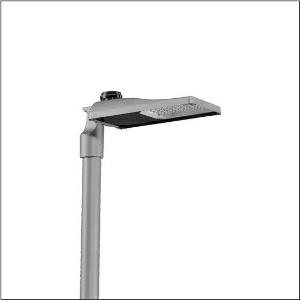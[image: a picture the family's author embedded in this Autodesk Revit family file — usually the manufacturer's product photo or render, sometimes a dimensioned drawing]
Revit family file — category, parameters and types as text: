
# Revit family: streetlight_sl_31_mini___st0_8a_5xh6c45n08ja_4560
name_source: partatom
category: Lighting Fixtures
units: mm (PartAtom-declared; Revit-internal decimal feet)

## family parameters
Cut with Voids When Loaded = No
Host = Face
Light Source = No
Part Type = Normal
Room Calculation Point = No
Round Connector Dimension = Use Diameter
Shared = No

## types (1)
- --- (1 x LED, 12590 lm, 81.1 W, 4000K)
    Apparent Load = 81 VA
    CIE Flux Codes = 41 75 97 100 100
    Color Rendering = 70
    Color Temperature = 4000K
    Default Elevation = 1800 mm
    Description = Streetlight SL 31 mini NEMA (7pin), Desk-Remote mast luminaire for post-top, side-entry; light control with lens of PMMA; light distribution: ST0.8a, direct asymmetric distribution, for standard-compliant lighting for roads and squares; LED: luminous flux: 12.590lm, light colour: 740, colour temperature: 4000K; luminous efficacy: 155,2lm/W; control: pre-setting: linear dimming characteristic, flexible luminous flux parameterisation, time-dependent luminous flux control, constant luminous flux control, intelligent temperature release in ECG and LED module, overheat protection; luminaire housing, of diecast aluminium, SITECO metallic grey (DB 702S), corrosivity category C5 high according to DIN EN ISO 12944; cover of toughened safety glass, transparent, opened without tools; mast flange of diecast aluminium, SITECO metallic grey (DB 702S), spigot size: 76/60mm, mast flange included unmounted; with cable H07RN-F 3x 1.5mm², cable length: 10,5m, connection cable pre-assembled; mains connection: 220..240V, AC, 50/60Hz; power consumption (at start of service life): 81,1W / (at end of service life): 88,3W / (with reduced operation 50%): 36,4W; protection rating (complete): IP66; insulation class (complete): insulation class I (protective earthing); impact resistance: IK10; certification: CE, ENEC, ENEC+, VDE, UKCA; permissible operating ambient temperature for outdoor applications: -40..+50°C; packaging unit: 1 piece

Light Distribution: ST0.8a
    Height = 76 mm
    Lamp = 1 x LED
    Lamp Light Flux = 12590 lm
    Lamp Power = 81.1 W
    Lamp count = 1
    Length = 547 mm
    Luminous efficacy = 155 lm/W
    Manufacturer = Siteco
    ModVariant = No
    Model = 5XH6C45N08JA
    Number of Poles = 1
    OnlyDefault = Yes
    Power Factor = 1
    Product Name = Streetlight SL 31 mini | ST0.8a
    Product group = mast luminaire | pylon top
    ProductGroupID = 6100
    Protection Class = Protection class I
    Protection Degree = IP 66
    RLX_Detail_Level = 1
    RLX_Emergency_Light_Flux = 0 lm
    RLX_Emergency_Type = 0
    RLX_Emergency_Type_DB = No
    RlxData = <blob elided: 40409 chars, md5=54567cdf>
    Socket = socket
    Standby Power = 0 W
    System Light Flux = 12590 lm
    System Power = 81 W
    Type Comments = factory setting: luminous flux: 100 % | dim-lin: 254 | 860 mA
    Type Image = l_1300322.jpg
    URL = http://relux.com
    VarID = @adj_056409
    Voltage = 0 V
    Weight = 0.00 kg
    Width = 265 mm

## geometry (parser evidence)
native form markers: Blend x4, Sweep x10
no freeform markers — native parametric forms only
